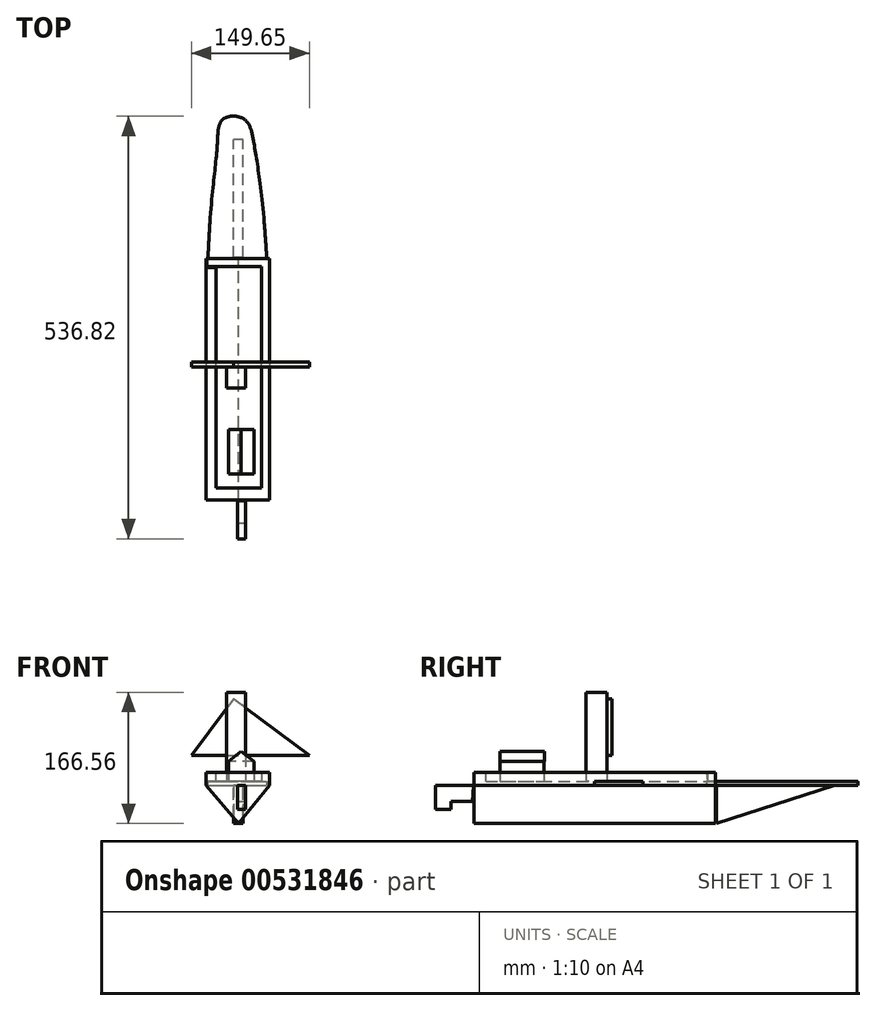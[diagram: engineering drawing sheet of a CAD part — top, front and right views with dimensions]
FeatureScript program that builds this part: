
annotation { "Feature Type Name" : "Feature", "Feature Type Description" : "" }
export const myFeature = defineFeature(function(context is Context, id is Id, definition is map)
    precondition{}
    {
        {
            var Q0;
            Q0=qCreatedBy(makeId("Top.planeOp"),FACE);
            var sketch = newSketch(context, id + "F0", { "sketchPlane" : qUnion([Q0])});
            skLineSegment(sketch, "E0.bottom", {"start": v(38.87, 56.39) * mm, "end": v(-30.2, 56.39) * mm});
            skLineSegment(sketch, "E0.top", {"start": v(38.87, -220.58) * mm, "end": v(-30.2, -220.58) * mm});
            skLineSegment(sketch, "E0.left", {"start": v(38.87, 56.39) * mm, "end": v(38.87, -220.58) * mm});
            skLineSegment(sketch, "E0.right", {"start": v(-30.2, 56.39) * mm, "end": v(-30.2, -220.58) * mm});
            skLineSegment(sketch, "E1.bottom", {"start": v(25.75, 56.39) * mm, "end": v(-20.67, 56.39) * mm});
            skLineSegment(sketch, "E1.top", {"start": v(25.75, 157.77) * mm, "end": v(-20.67, 157.77) * mm});
            skLineSegment(sketch, "E1.left", {"start": v(25.75, 56.39) * mm, "end": v(25.75, 157.77) * mm});
            skLineSegment(sketch, "E1.right", {"start": v(-20.67, 56.39) * mm, "end": v(-20.67, 157.77) * mm});
            skLineSegment(sketch, "E2.bottom", {"start": v(13.32, 157.77) * mm, "end": v(-13.46, 157.77) * mm});
            skLineSegment(sketch, "E2.top", {"start": v(13.32, 188.28) * mm, "end": v(-13.46, 188.28) * mm});
            skLineSegment(sketch, "E2.left", {"start": v(13.32, 157.77) * mm, "end": v(13.32, 188.28) * mm});
            skLineSegment(sketch, "E2.right", {"start": v(-13.46, 157.77) * mm, "end": v(-13.46, 188.28) * mm});
            skLineSegment(sketch, "E3.bottom", {"start": v(24.11, -220.58) * mm, "end": v(-8.56, -220.58) * mm});
            skLineSegment(sketch, "E3.top", {"start": v(24.11, -253.68) * mm, "end": v(-8.56, -253.68) * mm});
            skLineSegment(sketch, "E3.left", {"start": v(24.11, -220.58) * mm, "end": v(24.11, -253.68) * mm});
            skLineSegment(sketch, "E3.right", {"start": v(-8.56, -220.58) * mm, "end": v(-8.56, -253.68) * mm});
            skLineSegment(sketch, "E4.bottom", {"start": v(-20.67, -220.58) * mm, "end": v(-8.56, -220.58) * mm});
            skLineSegment(sketch, "E4.top", {"start": v(-20.67, -253.68) * mm, "end": v(-8.56, -253.68) * mm});
            skLineSegment(sketch, "E4.left", {"start": v(-20.67, -220.58) * mm, "end": v(-20.67, -253.68) * mm});
            skLineSegment(sketch, "E5.bottom", {"start": v(12.6, -253.68) * mm, "end": v(-8.56, -253.68) * mm});
            skLineSegment(sketch, "E5.top", {"start": v(12.6, -273.36) * mm, "end": v(-8.56, -273.36) * mm});
            skLineSegment(sketch, "E5.left", {"start": v(12.6, -253.68) * mm, "end": v(12.6, -273.36) * mm});
            skLineSegment(sketch, "E5.right", {"start": v(-8.56, -253.68) * mm, "end": v(-8.56, -273.36) * mm});
            skFitSpline(sketch, "E6", {"points": [v(-8.56, -273.36) * mm, v(-20.67, -253.68) * mm, v(-30.2, -220.58) * mm, v(-30.2, 56.39) * mm, v(-20.67, 157.77) * mm, v(-13.46, 188.28) * mm, v(13.32, 188.28) * mm, v(25.75, 157.77) * mm, v(38.87, 56.39) * mm, v(38.87, -220.58) * mm, v(24.11, -253.68) * mm, v(12.6, -273.36) * mm, v(-8.56, -273.36) * mm]});
            skSolve(sketch);
        }
        {
            var Q0;
            Q0=qCreatedBy(makeId("Front.planeOp"),FACE);
            var sketch = newSketch(context, id + "F1", { "sketchPlane" : qUnion([Q0])});
            skLineSegment(sketch, "E7", {"start": v(-35.12, 5.52) * mm, "end": v(-35.12, 0) * mm});
            skLineSegment(sketch, "E8", {"start": v(-35.12, 0) * mm, "end": v(5.95, -48) * mm});
            skLineSegment(sketch, "E9", {"start": v(5.95, -48) * mm, "end": v(45.6, 0) * mm});
            skLineSegment(sketch, "E10", {"start": v(45.6, 0) * mm, "end": v(45.6, 5.52) * mm});
            skLineSegment(sketch, "E11", {"start": v(45.6, 5.52) * mm, "end": v(-35.12, 5.52) * mm});
            skSolve(sketch);
        }
        {
            var Q0;
            Q0 = qSketchRegion(id + "F0", true);
            extrude(context, id + "F2", {"entities" : qUnion([Q0]), "depth" : 5.08 * mm, "offsetDistance" : 25.4 * mm});
        }
        {
            var Q0;
            Q0=makeQuery(id+"F1.imprint","IMPRINT",FACE,{"disambiguationData":[TD([[makeQuery(id+"F1.imprint","IMPRINT",EDGE,{"derivedFrom":sQuery(id+"F1.wireOp",EDGE,"E7")}),1.0]])]});
            extrude(context, id + "F3", {"entities" : qUnion([Q0]), "operationType" : NewBodyOperationType.ADD, "depth" : 295.66 * mm, "offsetDistance" : 25.4 * mm});
        }
        {
            var Q0;
            Q0=makeQuery(id+"F3.opExtrude","CAP_FACE",FACE,{"disambiguationData":[OSD([sQuery(id+"F1.wireOp",EDGE,"E7"),sQuery(id+"F1.wireOp",EDGE,"E8"),sQuery(id+"F1.wireOp",EDGE,"E9"),sQuery(id+"F1.wireOp",EDGE,"E10"),sQuery(id+"F1.wireOp",EDGE,"E11")])],"isStart":true});
            extrude(context, id + "F4", {"entities" : qUnion([Q0]), "operationType" : NewBodyOperationType.ADD, "depth" : 11.43 * mm, "offsetDistance" : 25.4 * mm});
        }
        {
            var Q0;
            {var subQ0=sQuery(id+"F1.wireOp",EDGE,"E11");Q0=makeQuery(id+"F4.boolean.opBoolean","MERGE",FACE,{"derivedFrom":[makeQuery(id+"F3.opExtrude","SWEPT_FACE",FACE,{"disambiguationData":[OSD([subQ0])]}),makeQuery(id+"F4.opExtrude","SWEPT_FACE",FACE,{"disambiguationData":[OSD([subQ0])]})]});}
            var sketch = newSketch(context, id + "F5", { "sketchPlane" : qUnion([Q0])});
            skLineSegment(sketch, "E12.bottom", {"start": v(15.2, -126.72) * mm, "end": v(-9.08, -126.72) * mm});
            skLineSegment(sketch, "E12.top", {"start": v(15.2, -153.02) * mm, "end": v(-9.08, -153.02) * mm});
            skLineSegment(sketch, "E12.left", {"start": v(15.2, -126.72) * mm, "end": v(15.2, -153.02) * mm});
            skLineSegment(sketch, "E12.right", {"start": v(-9.08, -126.72) * mm, "end": v(-9.08, -153.02) * mm});
            skSolve(sketch);
        }
        {
            var Q0;
            Q0 = qSketchRegion(id + "F5", true);
            extrude(context, id + "F6", {"entities" : qUnion([Q0]), "operationType" : NewBodyOperationType.ADD, "depth" : 113.03 * mm, "offsetDistance" : 25.4 * mm});
        }
        {
            var Q0;
            Q0=makeQuery(id+"Fh4IOYPSm67nbgI_1.boolean.opBoolean","MERGE",FACE,{"derivedFrom":[makeQuery(id+"F6.opExtrude","SWEPT_FACE",FACE,{"disambiguationData":[OSD([sQuery(id+"F5.wireOp",EDGE,"E12.left")])]}),makeQuery(id+"Fh4IOYPSm67nbgI_1.opExtrude","CAP_FACE",FACE,{"disambiguationData":[OSD([sQuery(id+"FlvdaMW9TVzW27Z_1.wireOp",EDGE,"1wYDknB8-vQ0h-26hZ-hZYw-cQyIdVzf7J6S"),sQuery(id+"FlvdaMW9TVzW27Z_1.wireOp",EDGE,"nUgxfpcG-S6f7-NfFj-7czA-1b6EkSgujqG4"),sQuery(id+"FlvdaMW9TVzW27Z_1.wireOp",EDGE,"Bs16cbXQ-4M0x-ZdKO-7Cit-GlM3yLBo8Y8L"),sQuery(id+"FlvdaMW9TVzW27Z_1.wireOp",EDGE,"kI8Sqf9P-KJAJ-wmjg-L6SH-lkx5ehk8jjBC")])],"isStart":true})]});
            var sketch = newSketch(context, id + "F7", { "sketchPlane" : qUnion([Q0])});
            skLineSegment(sketch, "E13", {"start": v(-295.98, 0) * mm, "end": v(-344.7, 0) * mm});
            skLineSegment(sketch, "E14", {"start": v(-344.7, 0) * mm, "end": v(-344.7, -30.35) * mm});
            skLineSegment(sketch, "E15", {"start": v(-344.7, -30.35) * mm, "end": v(-324.71, -30.35) * mm});
            skLineSegment(sketch, "E16", {"start": v(-324.71, -30.35) * mm, "end": v(-324.71, -20.36) * mm});
            skLineSegment(sketch, "E17", {"start": v(-324.71, -20.36) * mm, "end": v(-297.23, -20.36) * mm});
            skLineSegment(sketch, "E18", {"start": v(-297.23, -20.36) * mm, "end": v(-295.98, 0) * mm});
            skSolve(sketch);
        }
        {
            var Q0;
            Q0 = qSketchRegion(id + "F7", true);
            extrude(context, id + "F8", {"entities" : qUnion([Q0]), "oppositeDirection" : true, "depth" : 10.16 * mm, "offsetDistance" : 25.4 * mm});
        }
        {
            var Q0;
            Q0=makeQuery(id+"F3.opExtrude","CAP_FACE",FACE,{"disambiguationData":[OSD([sQuery(id+"F1.wireOp",EDGE,"E7"),sQuery(id+"F1.wireOp",EDGE,"E8"),sQuery(id+"F1.wireOp",EDGE,"E9"),sQuery(id+"F1.wireOp",EDGE,"E10"),sQuery(id+"F1.wireOp",EDGE,"E11")])],"isStart":false});
            var sketch = newSketch(context, id + "F9", { "sketchPlane" : qUnion([Q0])});
            skLineSegment(sketch, "E19", {"start": v(45.6, 5.52) * mm, "end": v(-35.12, 5.52) * mm});
            skLineSegment(sketch, "E20", {"start": v(-35.12, 5.52) * mm, "end": v(-35.12, 16.48) * mm});
            skLineSegment(sketch, "E21", {"start": v(-35.12, 16.48) * mm, "end": v(45.6, 16.48) * mm});
            skLineSegment(sketch, "E22", {"start": v(45.6, 16.48) * mm, "end": v(45.6, 5.52) * mm});
            skSolve(sketch);
        }
        {
            var Q0;
            Q0 = qSketchRegion(id + "F9", true);
            extrude(context, id + "F10", {"entities" : qUnion([Q0]), "operationType" : NewBodyOperationType.ADD, "oppositeDirection" : true, "depth" : 15.24 * mm, "offsetDistance" : 25.4 * mm});
        }
        {
            var Q0;
            {var subQ0=sQuery(id+"F1.wireOp",EDGE,"E10");Q0=makeQuery(id+"F10.boolean.opBoolean","MERGE",FACE,{"derivedFrom":[makeQuery(id+"F4.boolean.opBoolean","MERGE",FACE,{"derivedFrom":[makeQuery(id+"F3.opExtrude","SWEPT_FACE",FACE,{"disambiguationData":[OSD([subQ0])]}),makeQuery(id+"F4.opExtrude","SWEPT_FACE",FACE,{"disambiguationData":[OSD([subQ0])]})]}),makeQuery(id+"F10.opExtrude","SWEPT_FACE",FACE,{"disambiguationData":[OSD([sQuery(id+"F9.wireOp",EDGE,"E22")])]})]});}
            var sketch = newSketch(context, id + "F11", { "sketchPlane" : qUnion([Q0])});
            skLineSegment(sketch, "E23", {"start": v(-280.42, 16.48) * mm, "end": v(11.43, 16.48) * mm});
            skLineSegment(sketch, "E24", {"start": v(11.43, 16.48) * mm, "end": v(11.43, 0) * mm});
            skLineSegment(sketch, "E25", {"start": v(11.43, 0) * mm, "end": v(-280.42, 0) * mm});
            skLineSegment(sketch, "E26", {"start": v(-280.42, 0) * mm, "end": v(-280.42, 16.48) * mm});
            skSolve(sketch);
        }
        {
            var Q0;
            Q0 = qSketchRegion(id + "F11", true);
            extrude(context, id + "F12", {"entities" : qUnion([Q0]), "operationType" : NewBodyOperationType.ADD, "oppositeDirection" : true, "depth" : 10.16 * mm, "offsetDistance" : 25.4 * mm});
        }
        {
            var Q0;
            Q0=makeQuery(id+"F12.boolean.opBoolean","MERGE",FACE,{"derivedFrom":[makeQuery(id+"F4.opExtrude","CAP_FACE",FACE,{"disambiguationData":[OSD([sQuery(id+"F1.wireOp",EDGE,"E7"),sQuery(id+"F1.wireOp",EDGE,"E8"),sQuery(id+"F1.wireOp",EDGE,"E9"),sQuery(id+"F1.wireOp",EDGE,"E10"),sQuery(id+"F1.wireOp",EDGE,"E11")])],"isStart":false}),makeQuery(id+"F12.opExtrude","SWEPT_FACE",FACE,{"disambiguationData":[OSD([sQuery(id+"F11.wireOp",EDGE,"E24")])]})]});
            var sketch = newSketch(context, id + "F13", { "sketchPlane" : qUnion([Q0])});
            skLineSegment(sketch, "E27", {"start": v(-35.44, 16.48) * mm, "end": v(34.38, 16.48) * mm});
            skLineSegment(sketch, "E28", {"start": v(34.38, 16.48) * mm, "end": v(35.12, 5.52) * mm});
            skLineSegment(sketch, "E29", {"start": v(35.12, 5.52) * mm, "end": v(-35.44, 5.52) * mm});
            skLineSegment(sketch, "E30", {"start": v(-35.44, 5.52) * mm, "end": v(-35.44, 16.48) * mm});
            skSolve(sketch);
        }
        {
            var Q0;
            Q0 = qSketchRegion(id + "F13", true);
            extrude(context, id + "F14", {"entities" : qUnion([Q0]), "operationType" : NewBodyOperationType.ADD, "oppositeDirection" : true, "depth" : 10.16 * mm, "offsetDistance" : 25.4 * mm});
        }
        {
            var Q0;
            {var subQ0=sQuery(id+"F1.wireOp",EDGE,"E7");Q0=makeQuery(id+"F10.boolean.opBoolean","MERGE",FACE,{"derivedFrom":[makeQuery(id+"F4.boolean.opBoolean","MERGE",FACE,{"derivedFrom":[makeQuery(id+"F3.opExtrude","SWEPT_FACE",FACE,{"disambiguationData":[OSD([subQ0])]}),makeQuery(id+"F4.opExtrude","SWEPT_FACE",FACE,{"disambiguationData":[OSD([subQ0])]})]}),makeQuery(id+"F10.opExtrude","SWEPT_FACE",FACE,{"disambiguationData":[OSD([sQuery(id+"F9.wireOp",EDGE,"E20")])]})]});}
            var sketch = newSketch(context, id + "F15", { "sketchPlane" : qUnion([Q0])});
            skLineSegment(sketch, "E31", {"start": v(-1.27, 5.52) * mm, "end": v(280.42, 5.52) * mm});
            skLineSegment(sketch, "E32", {"start": v(280.42, 5.52) * mm, "end": v(280.42, 16.48) * mm});
            skLineSegment(sketch, "E33", {"start": v(280.42, 16.48) * mm, "end": v(0, 16.48) * mm});
            skLineSegment(sketch, "E34", {"start": v(0, 16.48) * mm, "end": v(-1.27, 5.52) * mm});
            skSolve(sketch);
        }
        {
            var Q0;
            Q0 = qSketchRegion(id + "F15", true);
            extrude(context, id + "F16", {"entities" : qUnion([Q0]), "operationType" : NewBodyOperationType.ADD, "oppositeDirection" : true, "depth" : 12.7 * mm, "offsetDistance" : 25.4 * mm});
        }
        {
            var Q0;
            Q0=makeQuery(id+"F6.opExtrude","SWEPT_FACE",FACE,{"disambiguationData":[OSD([sQuery(id+"F5.wireOp",EDGE,"E12.bottom")])]});
            var sketch = newSketch(context, id + "F17", { "sketchPlane" : qUnion([Q0])});
            skLineSegment(sketch, "E35", {"start": v(-15.2, 38.4) * mm, "end": v(-96.16, 38.4) * mm});
            skLineSegment(sketch, "E36", {"start": v(-96.16, 38.4) * mm, "end": v(0, 110.12) * mm});
            skLineSegment(sketch, "E37", {"start": v(0, 110.12) * mm, "end": v(53.5, 38.4) * mm});
            skLineSegment(sketch, "E38", {"start": v(53.5, 38.4) * mm, "end": v(-15.2, 38.4) * mm});
            skSolve(sketch);
        }
        {
            var Q0;
            Q0 = qSketchRegion(id + "F17", true);
            extrude(context, id + "F18", {"entities" : qUnion([Q0]), "operationType" : NewBodyOperationType.ADD, "depth" : 6.6 * mm, "offsetDistance" : 25.4 * mm});
        }
        {
            var Q0;
            {var subQ0=sQuery(id+"F1.wireOp",EDGE,"E11");Q0=makeQuery(id+"F4.boolean.opBoolean","MERGE",FACE,{"derivedFrom":[makeQuery(id+"F3.opExtrude","SWEPT_FACE",FACE,{"disambiguationData":[OSD([subQ0])]}),makeQuery(id+"F4.opExtrude","SWEPT_FACE",FACE,{"disambiguationData":[OSD([subQ0])]})]});}
            var sketch = newSketch(context, id + "F19", { "sketchPlane" : qUnion([Q0])});
            skLineSegment(sketch, "E39.bottom", {"start": v(26.03, -262.72) * mm, "end": v(-6.51, -262.72) * mm});
            skLineSegment(sketch, "E39.top", {"start": v(26.03, -206.36) * mm, "end": v(-6.51, -206.36) * mm});
            skLineSegment(sketch, "E39.left", {"start": v(26.03, -262.72) * mm, "end": v(26.03, -206.36) * mm});
            skLineSegment(sketch, "E39.right", {"start": v(-6.51, -262.72) * mm, "end": v(-6.51, -206.36) * mm});
            skSolve(sketch);
        }
        {
            var Q0;
            Q0 = qSketchRegion(id + "F19", true);
            extrude(context, id + "F20", {"entities" : qUnion([Q0]), "operationType" : NewBodyOperationType.ADD, "depth" : 25.4 * mm, "offsetDistance" : 25.4 * mm});
        }
        {
            var Q0;
            Q0=makeQuery(id+"F20.opExtrude","SWEPT_FACE",FACE,{"disambiguationData":[OSD([sQuery(id+"F19.wireOp",EDGE,"E39.bottom")])]});
            var sketch = newSketch(context, id + "F21", { "sketchPlane" : qUnion([Q0])});
            skLineSegment(sketch, "E40", {"start": v(-6.51, 30.92) * mm, "end": v(9.68, 43.17) * mm});
            skLineSegment(sketch, "E41", {"start": v(9.68, 43.17) * mm, "end": v(26.03, 30.92) * mm});
            skLineSegment(sketch, "E42", {"start": v(26.03, 30.92) * mm, "end": v(-6.51, 30.92) * mm});
            skSolve(sketch);
        }
        {
            var Q0;
            Q0=makeQuery(id+"F21.imprint","IMPRINT",FACE,{"disambiguationData":[TD([[makeQuery(id+"F21.imprint","IMPRINT",EDGE,{"derivedFrom":sQuery(id+"F21.wireOp",EDGE,"E40")}),-1.0]])]});
            extrude(context, id + "F22", {"entities" : qUnion([Q0]), "operationType" : NewBodyOperationType.ADD, "oppositeDirection" : true, "depth" : 56.9 * mm, "offsetDistance" : 25.4 * mm});
        }
        {
            var Q0;
            Q0=qCreatedBy(makeId("Right.planeOp"),FACE);
            var sketch = newSketch(context, id + "F23", { "sketchPlane" : qUnion([Q0])});
            skLineSegment(sketch, "E43", {"start": v(12.38, 0) * mm, "end": v(162.23, 0) * mm});
            skLineSegment(sketch, "E44", {"start": v(162.23, 0) * mm, "end": v(12.38, -47.9) * mm});
            skLineSegment(sketch, "E45", {"start": v(12.38, -47.9) * mm, "end": v(12.38, 0) * mm});
            skSolve(sketch);
        }
        {
            var Q0;
            Q0 = qSketchRegion(id + "F23", true);
            extrude(context, id + "F24", {"entities" : qUnion([Q0]), "operationType" : NewBodyOperationType.ADD, "depth" : 11.68 * mm, "offsetDistance" : 25.4 * mm});
        }
    });
